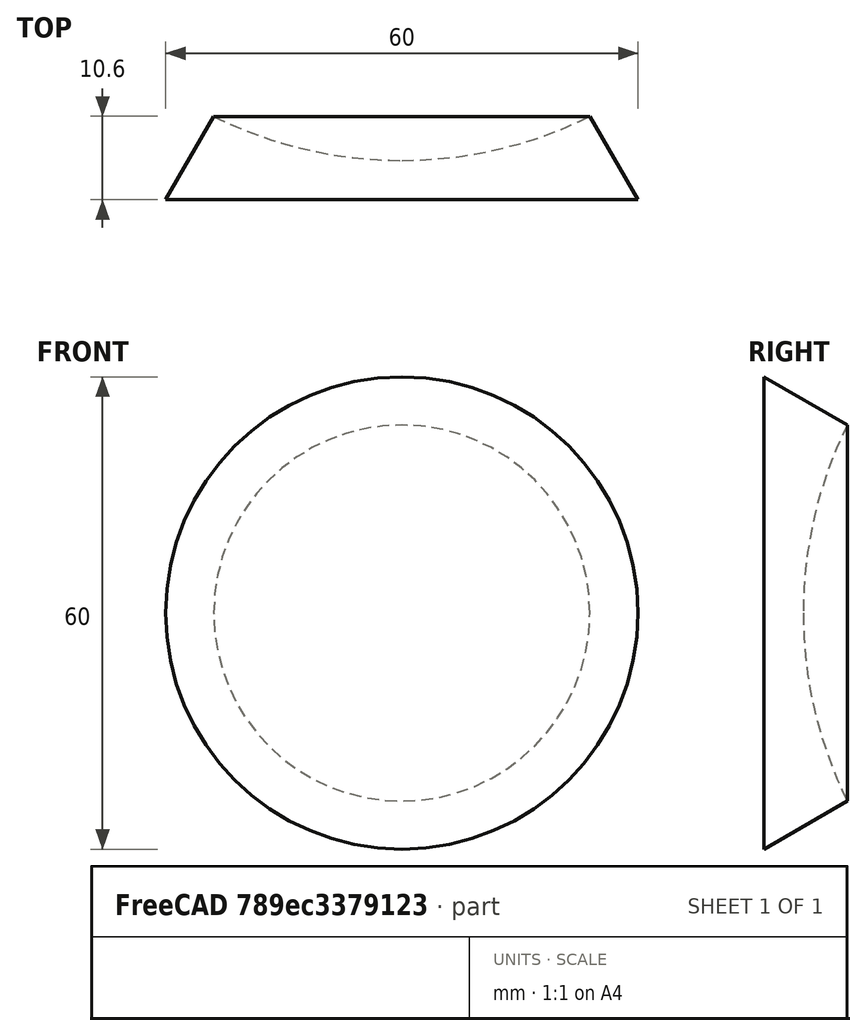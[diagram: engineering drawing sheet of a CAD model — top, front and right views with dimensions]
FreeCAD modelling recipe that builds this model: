
FCSTD DOCUMENT  (FreeCAD 2022.111R30764 (Git))
Label: dresser drawer leveler
License: All rights reserved
LicenseURL: http://en.wikipedia.org/wiki/All_rights_reserved
objects: Sketcher::SketchObject×1, PartDesign::Revolution×1, PartDesign::Body×1
note: 5 computed .brp shape members not serialized (recipe doc carries the construction recipe); baked Part::Feature solids carry a one-line shape summary decoded from their .brp

FEATURE [Sketcher::SketchObject] Sketch
  FullyConstrained = true
  MapMode = 5
  Support = -> [XY_Plane]
  TreeRank = 11
  sketch-geometry (4):
    g0: ArcOfCircle CenterX=0 CenterY=58.76 CenterZ=0 NormalX=0 NormalY=0 NormalZ=1 AngleXU=0 Radius=53.76 StartAngle=4.71239 EndAngle=5.17272
    g1: LineSegment StartX=0 StartY=0 StartZ=0 EndX=30 EndY=0 EndZ=0
    g2: LineSegment StartX=30 StartY=0 StartZ=0 EndX=23.8824 EndY=10.596 EndZ=0
    g3: LineSegment StartX=-9.9e-15 StartY=5 StartZ=0 EndX=0 EndY=0 EndZ=0
  constraints (12):
    c: PointOnObject(g1,g-1)
    c: Coincident(g1,g2)
    c: Coincident(g2,g0)
    c: DistanceY(g1,g0) = 5
    c: PointOnObject(g0,g-2)
    c: Angle(g2,g1) = 1.0472
    c: Coincident(g1,g-1)
    c: DistanceX(g1,g1) = 30
    c: PointOnObject(g0,g-2)
    c: Diameter(g0) = 107.52
    c: Coincident(g3,g0)
    c: Coincident(g3,g1)
FEATURE [PartDesign::Revolution] Revolution
  AddSubType = 0
  Angle = 360
  Axis = (0,1,0)
  Base = (0,0,0)
  ClaimChildren = false
  Fit = 0
  FitJoin = 0
  InnerFit = 0
  InnerFitJoin = 0
  Linearize = true
  NewSolid = false
  Profile = -> Sketch
  ReferenceAxis = -> Sketch [V_Axis]
  Reversed = true
  Suppress = false
  TreeRank = 12
  _ProfileBasedVersion = 1
FEATURE [PartDesign::Body] Body
  AutoGroupSolids = false
  ExportMode = 0
  Group = -> [Sketch,Revolution]
  Origin = -> Origin
  Tip = -> Revolution
  TreeRank = 10
  _ExportChildren = -> [Revolution]
  _GroupVersion = 1
